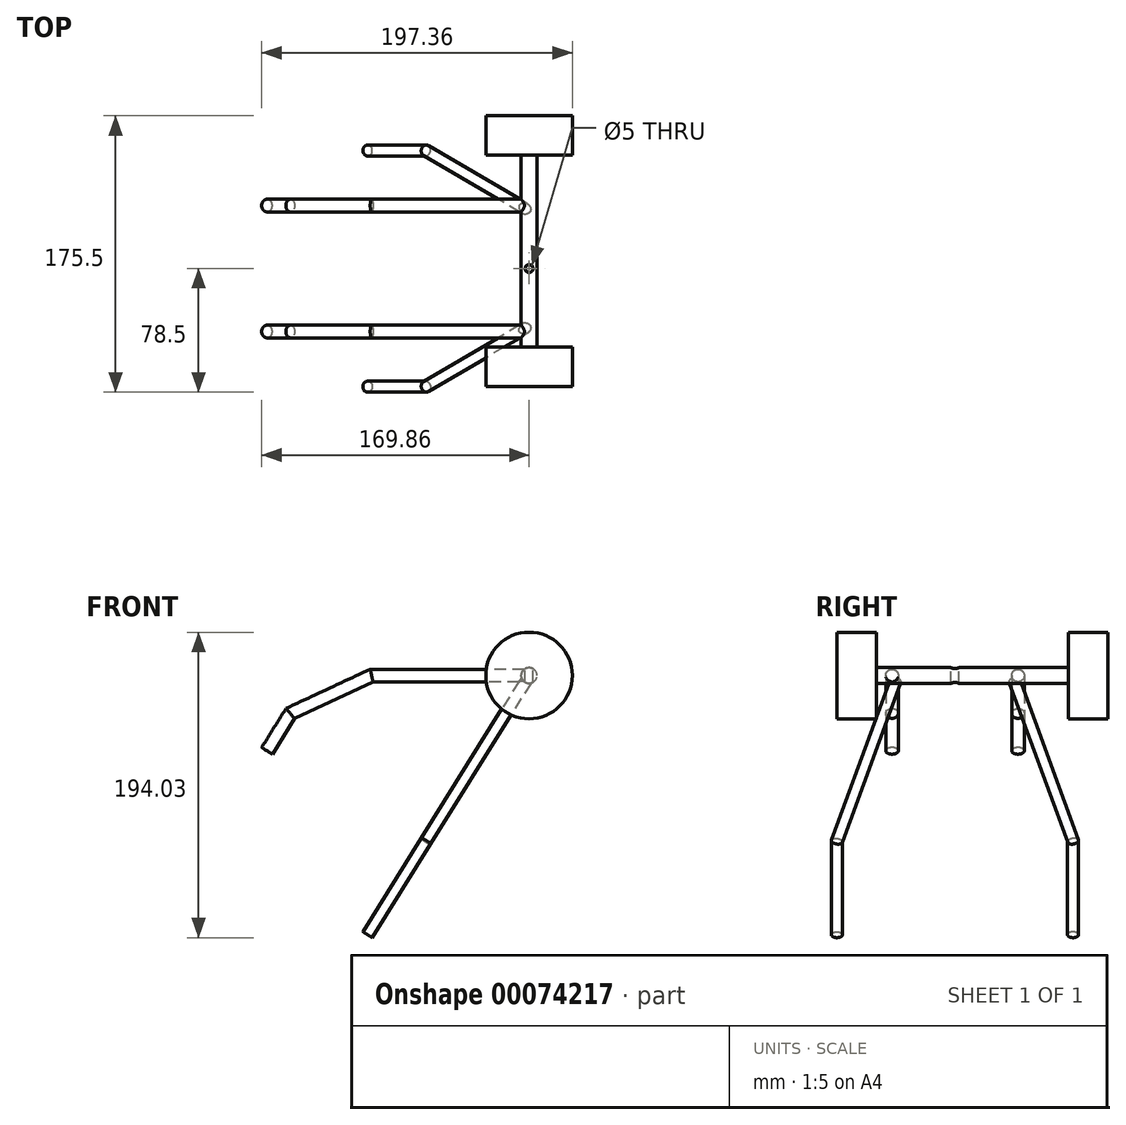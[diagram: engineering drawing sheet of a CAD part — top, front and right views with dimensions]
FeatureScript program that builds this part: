
annotation { "Feature Type Name" : "Feature", "Feature Type Description" : "" }
export const myFeature = defineFeature(function(context is Context, id is Id, definition is map)
    precondition{}
    {
        {
            var Q0;
            Q0=qCreatedBy(makeId("Front.planeOp"),FACE);
            cPlane(context, id + "F0", {"entities" : qUnion([Q0]), "cplaneType" : CPlaneType.OFFSET, "offset" : 88 * mm, "width" : 150 * mm, "height" : 150 * mm});
        }
        {
            var Q0;
            Q0=qCreatedBy(makeId("Front.planeOp"),FACE);
            var sketch = newSketch(context, id + "F1", { "sketchPlane" : qUnion([Q0])});
            skLineSegment(sketch, "E0", {"start": v(0, 0) * mm, "end": v(-100, 0) * mm});
            skLineSegment(sketch, "E1", {"start": v(-100, 0) * mm, "end": v(-151.66, -24.09) * mm});
            skLineSegment(sketch, "E2", {"start": v(-151.66, -24.09) * mm, "end": v(-166.46, -47.86) * mm});
            skSolve(sketch);
        }
        {
            var Q0;
            Q0=qCreatedBy(makeId("Right.planeOp"),FACE);
            var sketch = newSketch(context, id + "F2", { "sketchPlane" : qUnion([Q0])});
            skCircle(sketch, "E3", {"center": v(-4, 0) * mm, "radius": 4 * mm});
            skCircle(sketch, "E4", {"center": v(-84, 0) * mm, "radius": 4 * mm});
            skSolve(sketch);
        }
        {
            var Q0;
            Q0 = qSketchRegion(id + "F2", true);
            var Q1;
            Q1 = qConstructionFilter(qBodyType(qCreatedBy(id + "F1" ,EDGE), BodyType.WIRE), ConstructionObject.NO);
            sweep(context, id + "F3", {"profiles" : qUnion([Q0]), "path" : qUnion([Q1])});
        }
        {
            var Q0;
            Q0=qCreatedBy(makeId("Front.planeOp"),FACE);
            var Q1;
            Q1=qCreatedBy(id+"F0.planeOp",FACE);
            cPlane(context, id + "F4", {"entities" : qUnion([Q0, Q1]), "cplaneType" : CPlaneType.MID_PLANE, "offset" : 150 * mm, "width" : 150 * mm, "height" : 150 * mm});
        }
        {
            var Q0;
            Q0=qCreatedBy(id+"F4.planeOp",FACE);
            var sketch = newSketch(context, id + "F5", { "sketchPlane" : qUnion([Q0])});
            skCircle(sketch, "E5", {"center": v(0, 0) * mm, "radius": 5 * mm});
            skSolve(sketch);
        }
        {
            var Q0;
            Q0=makeQuery(id+"F3.opSweep","SWEPT_FACE",FACE,{"disambiguationData":[OSD([sQuery(id+"F1.wireOp",EDGE,"E2"),sQuery(id+"F2.wireOp",EDGE,"E3")])]});
            cPlane(context, id + "F6", {"entities" : qUnion([Q0]), "cplaneType" : CPlaneType.LINE_ANGLE, "offset" : 150 * mm, "angle" : 0 * degree, "width" : 150 * mm, "height" : 150 * mm});
        }
        {
            var Q0;
            Q0=qCreatedBy(id+"F6.planeOp",FACE);
            var Q1;
            Q1=sQuery(id+"F1.wireOp",VERTEX,"E0.start");
            cPlane(context, id + "F7", {"entities" : qUnion([Q0, Q1]), "cplaneType" : CPlaneType.PLANE_POINT, "offset" : 150 * mm, "width" : 150 * mm, "height" : 150 * mm});
        }
        {
            var Q0;
            Q0=qCreatedBy(id+"F7.planeOp",FACE);
            var sketch = newSketch(context, id + "F8", { "sketchPlane" : qUnion([Q0])});
            skLineSegment(sketch, "E6", {"start": v(80.5, 0) * mm, "end": v(119, -124) * mm});
            skLineSegment(sketch, "E7", {"start": v(119, -124) * mm, "end": v(119, -194) * mm});
            skLineSegment(sketch, "E8", {"start": v(80.5, 0) * mm, "end": v(44, 0) * mm});
            skSolve(sketch);
        }
        {
            var Q0;
            Q0=qCreatedBy(id+"F4.planeOp",FACE);
            var sketch = newSketch(context, id + "F9", { "sketchPlane" : qUnion([Q0])});
            skCircle(sketch, "E9", {"center": v(0, 0) * mm, "radius": 3.5 * mm});
            skSolve(sketch);
        }
        {
            var Q0;
            Q0 = qSketchRegion(id + "F9", true);
            var Q1;
            Q1 = qConstructionFilter(qBodyType(qCreatedBy(id + "F8" ,EDGE), BodyType.WIRE), ConstructionObject.NO);
            sweep(context, id + "F10", {"operationType" : NewBodyOperationType.ADD, "profiles" : qUnion([Q0]), "path" : qUnion([Q1])});
        }
        {
            var Q0;
            Q0=makeQuery(id+"F3.opSweep","SWEPT_BODY",BODY,{"disambiguationData":[OSD([sQuery(id+"F1.wireOp",EDGE,"E2"),sQuery(id+"F2.wireOp",EDGE,"E4")])]});
            var Q1;
            Q1=qCreatedBy(id+"F4.planeOp",FACE);
            mirror(context, id + "F11", {"operationType" : NewBodyOperationType.ADD, "entities" : qUnion([Q0]), "mirrorPlane" : qUnion([Q1])});
        }
        {
            var Q0;
            Q0 = qSketchRegion(id + "F5", true);
            extrude(context, id + "F12", {"entities" : qUnion([Q0]), "operationType" : NewBodyOperationType.ADD, "depth" : 50 * mm, "hasSecondDirection" : true, "secondDirectionOppositeDirection" : true, "secondDirectionDepth" : 72 * mm});
        }
        {
            var Q0;
            Q0=qCreatedBy(makeId("Top.planeOp"),FACE);
            var sketch = newSketch(context, id + "F13", { "sketchPlane" : qUnion([Q0])});
            skCircle(sketch, "E10", {"center": v(0, -44) * mm, "radius": 2.5 * mm});
            skSolve(sketch);
        }
        {
            var Q0;
            Q0 = qSketchRegion(id + "F13", true);
            extrude(context, id + "F14", {"entities" : qUnion([Q0]), "operationType" : NewBodyOperationType.REMOVE, "endBound" : BoundingType.THROUGH_ALL, "oppositeDirection" : true, "depth" : 25 * mm, "hasSecondDirection" : true, "secondDirectionBound" : SecondDirectionBoundingType.THROUGH_ALL, "secondDirectionOppositeDirection" : false, "secondDirectionDepth" : 25 * mm});
        }
        {
            var Q0;
            Q0=makeQuery(id+"F12.opExtrude","CAP_FACE",FACE,{"disambiguationData":[OSD([sQuery(id+"F5.wireOp",EDGE,"E5")])],"isStart":false});
            var sketch = newSketch(context, id + "F15", { "sketchPlane" : qUnion([Q0])});
            skCircle(sketch, "E11", {"center": v(0, 0) * mm, "radius": 27.5 * mm});
            skSolve(sketch);
        }
        {
            var Q0;
            Q0 = qSketchRegion(id + "F15", true);
            extrude(context, id + "F16", {"entities" : qUnion([Q0]), "operationType" : NewBodyOperationType.ADD, "depth" : 25 * mm});
        }
        {
            var Q0;
            Q0=makeQuery(id+"F12.opExtrude","CAP_FACE",FACE,{"disambiguationData":[OSD([sQuery(id+"F5.wireOp",EDGE,"E5")])],"isStart":true});
            var sketch = newSketch(context, id + "F17", { "sketchPlane" : qUnion([Q0])});
            skCircle(sketch, "E12", {"center": v(0, 0) * mm, "radius": 27.5 * mm});
            skSolve(sketch);
        }
        {
            var Q0;
            Q0 = qSketchRegion(id + "F17", true);
            extrude(context, id + "F18", {"entities" : qUnion([Q0]), "operationType" : NewBodyOperationType.ADD, "depth" : 25 * mm});
        }
    });
